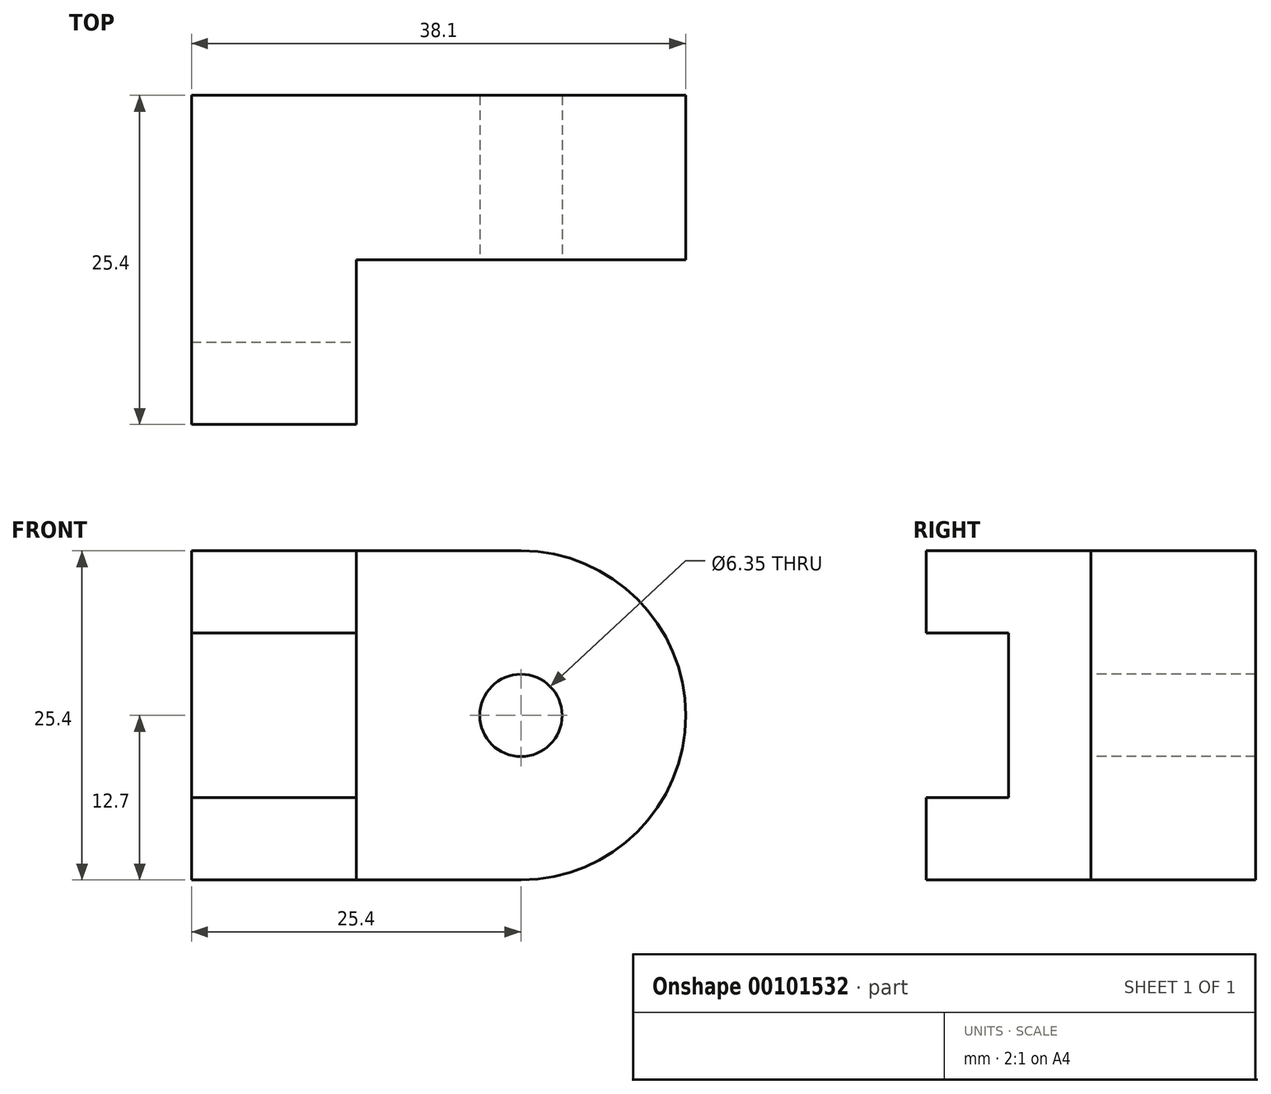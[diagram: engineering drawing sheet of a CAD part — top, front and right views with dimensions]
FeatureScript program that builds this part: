
annotation { "Feature Type Name" : "Feature", "Feature Type Description" : "" }
export const myFeature = defineFeature(function(context is Context, id is Id, definition is map)
    precondition{}
    {
        {
            var Q0;
            Q0=qCreatedBy(makeId("Front.planeOp"),FACE);
            var sketch = newSketch(context, id + "F0", { "sketchPlane" : qUnion([Q0])});
            skLineSegment(sketch, "E0", {"start": v(0, 0) * mm, "end": v(0, 25.4) * mm});
            skLineSegment(sketch, "E1", {"start": v(0, 25.4) * mm, "end": v(12.7, 25.4) * mm});
            skLineSegment(sketch, "E2", {"start": v(12.7, 25.4) * mm, "end": v(12.7, 0) * mm});
            skLineSegment(sketch, "E3", {"start": v(12.7, 0) * mm, "end": v(0, 0) * mm});
            skSolve(sketch);
        }
        {
            var Q0;
            Q0 = qSketchRegion(id + "F0", true);
            extrude(context, id + "F1", {"entities" : qUnion([Q0]), "depth" : 25.4 * mm});
        }
        {
            var Q0;
            Q0=makeQuery(id+"F1.opExtrude","CAP_FACE",FACE,{"disambiguationData":[OSD([sQuery(id+"F0.wireOp",EDGE,"E0"),sQuery(id+"F0.wireOp",EDGE,"E1"),sQuery(id+"F0.wireOp",EDGE,"E2"),sQuery(id+"F0.wireOp",EDGE,"E3")])],"isStart":true});
            var sketch = newSketch(context, id + "F2", { "sketchPlane" : qUnion([Q0])});
            skLineSegment(sketch, "E4", {"start": v(-12.7, 25.4) * mm, "end": v(-25.4, 25.4) * mm});
            skLineSegment(sketch, "E5", {"start": v(-12.7, 0) * mm, "end": v(-25.4, 0) * mm});
            skArc(sketch, "E6", {"start": v(-25.4, 25.4) * mm, "mid": v(-38.1, 12.7) * mm, "end": v(-25.4, 0) * mm});
            skSolve(sketch);
        }
        {
            var Q0;
            Q0 = qSketchRegion(id + "F2", true);
            var Q1;
            Q1=makeQuery(id+"F2.imprint","IMPRINT",FACE,{"disambiguationData":[TD([[makeQuery(id+"F2.imprint","IMPRINT",EDGE,{"derivedFrom":sQuery(id+"F2.wireOp",EDGE,"E4")}),1.0]])]});
            extrude(context, id + "F3", {"entities" : qUnion([Q0, Q1]), "operationType" : NewBodyOperationType.ADD, "oppositeDirection" : true, "depth" : 12.7 * mm});
        }
        {
            var Q0;
            Q0=makeQuery(id+"F1.opExtrude","CAP_FACE",FACE,{"disambiguationData":[OSD([sQuery(id+"F0.wireOp",EDGE,"E0"),sQuery(id+"F0.wireOp",EDGE,"E1"),sQuery(id+"F0.wireOp",EDGE,"E2"),sQuery(id+"F0.wireOp",EDGE,"E3")])],"isStart":false});
            var sketch = newSketch(context, id + "F4", { "sketchPlane" : qUnion([Q0])});
            skLineSegment(sketch, "E7", {"start": v(0, 19.05) * mm, "end": v(12.7, 19.05) * mm});
            skLineSegment(sketch, "E8", {"start": v(12.7, 19.05) * mm, "end": v(12.7, 6.35) * mm});
            skLineSegment(sketch, "E9", {"start": v(12.7, 6.35) * mm, "end": v(0, 6.35) * mm});
            skLineSegment(sketch, "E10", {"start": v(0, 6.35) * mm, "end": v(0, 19.05) * mm});
            skSolve(sketch);
        }
        {
            var Q0;
            Q0 = qSketchRegion(id + "F4", true);
            extrude(context, id + "F5", {"entities" : qUnion([Q0]), "operationType" : NewBodyOperationType.REMOVE, "oppositeDirection" : true, "depth" : 6.35 * mm});
        }
        {
            var Q0;
            Q0=makeQuery(id+"F3.opExtrude","CAP_FACE",FACE,{"disambiguationData":[OSD([sQuery(id+"F0.wireOp",EDGE,"E2"),sQuery(id+"F2.wireOp",EDGE,"E4"),sQuery(id+"F2.wireOp",EDGE,"E5"),sQuery(id+"F2.wireOp",EDGE,"E6")])],"isStart":false});
            var sketch = newSketch(context, id + "F6", { "sketchPlane" : qUnion([Q0])});
            skCircle(sketch, "E11", {"center": v(25.4, 12.7) * mm, "radius": 3.18 * mm});
            skSolve(sketch);
        }
        {
            var Q0;
            Q0 = qSketchRegion(id + "F6", true);
            extrude(context, id + "F7", {"entities" : qUnion([Q0]), "operationType" : NewBodyOperationType.REMOVE, "endBound" : BoundingType.UP_TO_NEXT, "oppositeDirection" : true, "depth" : 25.4 * mm});
        }
    });
